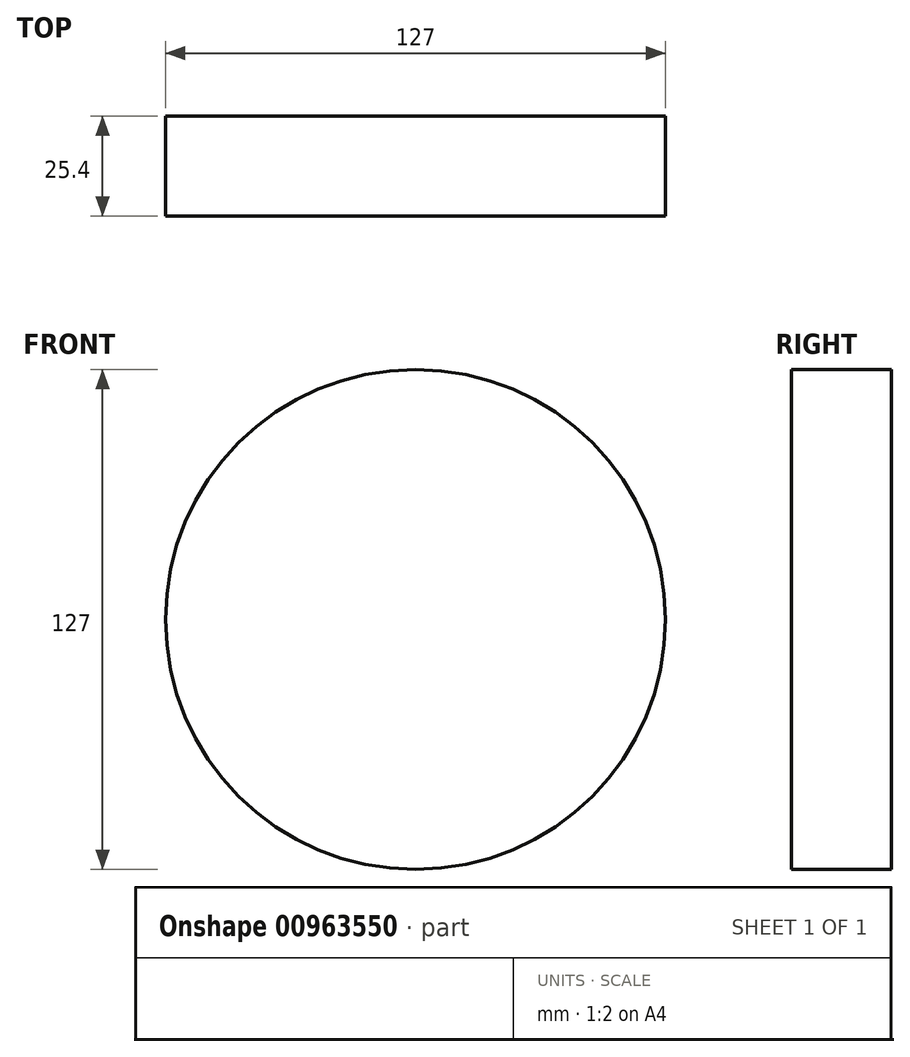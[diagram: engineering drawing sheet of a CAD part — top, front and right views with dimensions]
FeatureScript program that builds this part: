
annotation { "Feature Type Name" : "Feature", "Feature Type Description" : "" }
export const myFeature = defineFeature(function(context is Context, id is Id, definition is map)
    precondition{}
    {
        {
            var Q0;
            Q0=qCreatedBy(makeId("Front.planeOp"),FACE);
            var sketch = newSketch(context, id + "F0", { "sketchPlane" : qUnion([Q0])});
            skCircle(sketch, "E0", {"center": v(0, 0) * mm, "radius": 63.5 * mm});
            skSolve(sketch);
        }
        {
            var Q0;
            Q0 = qSketchRegion(id + "F0", true);
            extrude(context, id + "F1", {"entities" : qUnion([Q0]), "depth" : 25.4 * mm, "offsetDistance" : 25.4 * mm});
        }
    });
